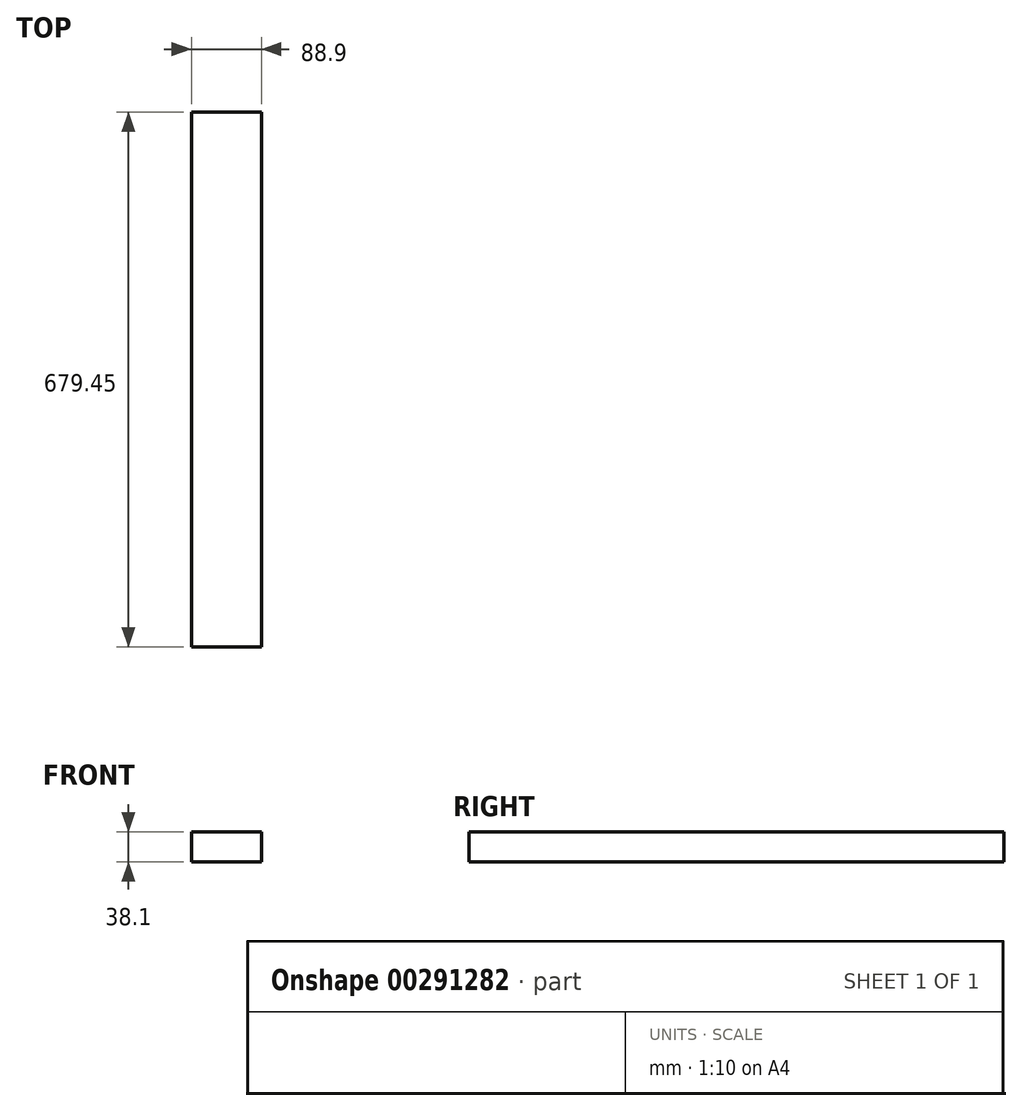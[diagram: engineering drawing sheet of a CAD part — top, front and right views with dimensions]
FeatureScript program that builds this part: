
annotation { "Feature Type Name" : "Feature", "Feature Type Description" : "" }
export const myFeature = defineFeature(function(context is Context, id is Id, definition is map)
    precondition{}
    {
        {
            var Q0;
            Q0=qCreatedBy(makeId("Front.planeOp"),FACE);
            var sketch = newSketch(context, id + "F0", { "sketchPlane" : qUnion([Q0])});
            skLineSegment(sketch, "E0", {"start": v(44.45, 19.05) * mm, "end": v(44.45, -19.05) * mm});
            skLineSegment(sketch, "E1", {"start": v(44.45, -19.05) * mm, "end": v(-44.45, -19.05) * mm});
            skLineSegment(sketch, "E2", {"start": v(-44.45, -19.05) * mm, "end": v(-44.45, 19.05) * mm});
            skLineSegment(sketch, "E3", {"start": v(-44.45, 19.05) * mm, "end": v(44.45, 19.05) * mm});
            skSolve(sketch);
        }
        {
            var Q0;
            Q0 = qSketchRegion(id + "F0", true);
            extrude(context, id + "F1", {"entities" : qUnion([Q0]), "depth" : 679.45 * mm});
        }
    });
